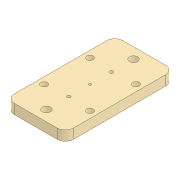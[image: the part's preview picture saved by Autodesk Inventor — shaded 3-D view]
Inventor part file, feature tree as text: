
AUTODESK INVENTOR PART (.ipt)
format: ipt  version: 2020 (Build 240168000, 168)  size: 148,992 bytes
history: native  units: mm
features: extrude x3, sketch x3, other x1, chamfer x1, fillet x1
ambient origin geometry x8: Origin, YZ Plane, XZ Plane, XY Plane, X Axis, Y Axis, Z Axis, Center Point
bodies: Body1 (feature_tree)
feature tree (9):
  other  "Sólido1"
  extrude  "Extrusão1"  Depth=12.0mm TaperAngle=0.0deg
  extrude  "Extrusão2"  Depth=4.2mm
  chamfer  "Chanfro1"  Distance=12.0mm
  fillet  "Arredondamento1"  Radius=2.5mm
  extrude  "Extrusão3"  Depth=132.363mm
  sketch  "Esboço1"  dims[d0=69.9mm d1=12.0mm d2=0.0mm]
  sketch  "Esboço2"  dims[d3=3.0mm d4=4.2mm]
  sketch  "Esboço3"  dims[d5=4.2mm d6=12.0mm d7=0.0mm d8=2.5mm d9=2.0mm d10=45.0deg d11=132.363mm d12=72.0mm d13=10.0mm d14=53.1mm d15=10.0mm d16=53.1mm d20=52.0mm d21=10.0mm d22=8.0mm d23=28.0mm d24=28.0mm d25=20.0mm d27=56.0mm d28=20.0mm d30=56.0mm d33=12.0mm d34=0.0mm]
